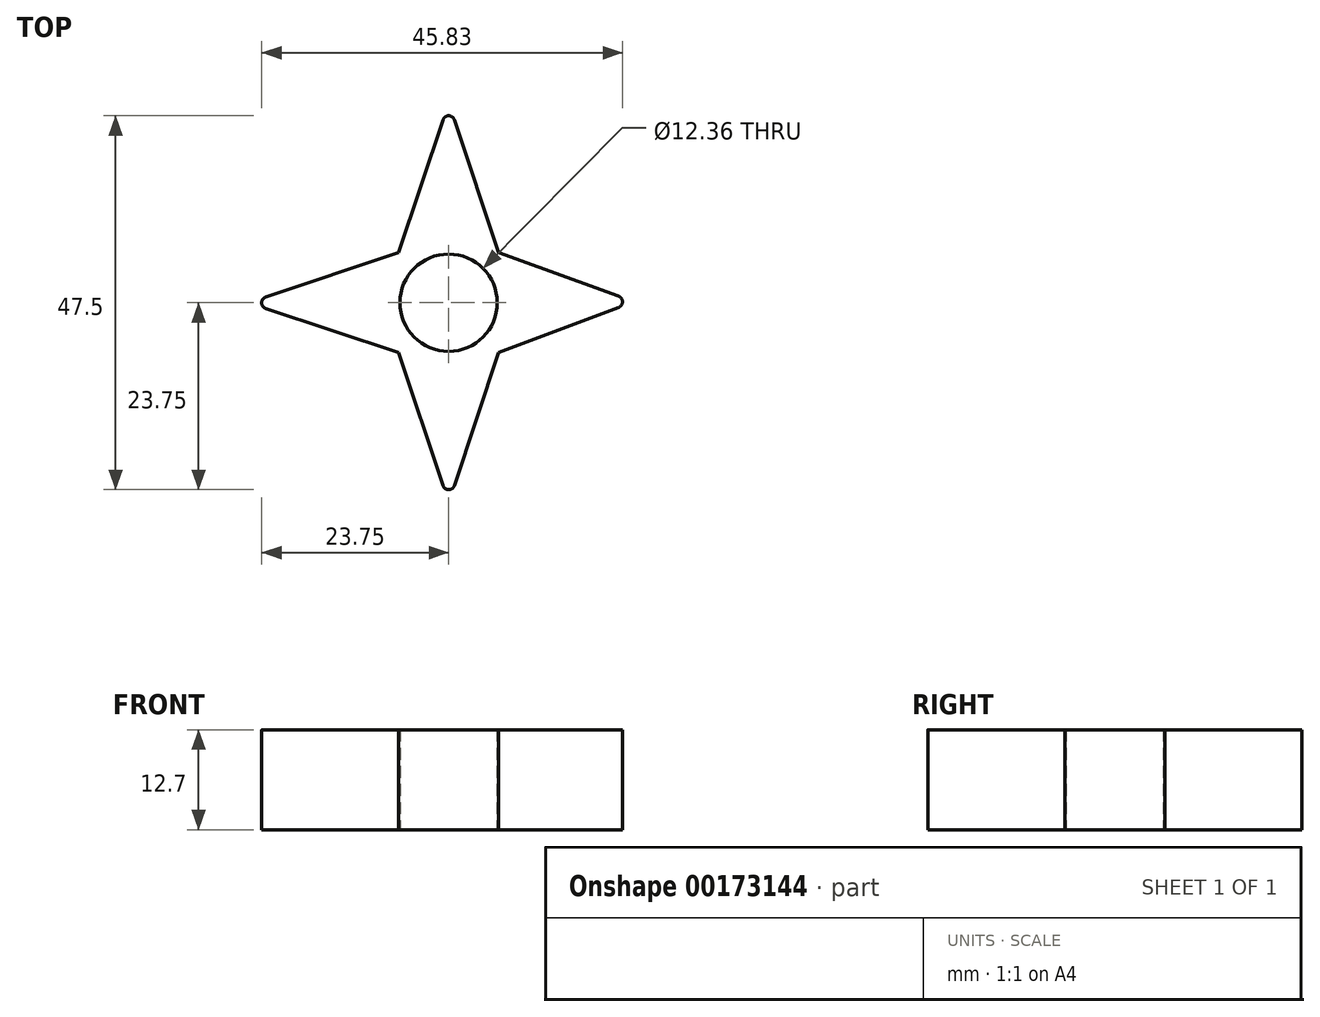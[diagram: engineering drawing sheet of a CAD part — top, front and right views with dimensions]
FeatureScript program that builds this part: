
annotation { "Feature Type Name" : "Feature", "Feature Type Description" : "" }
export const myFeature = defineFeature(function(context is Context, id is Id, definition is map)
    precondition{}
    {
        {
            var Q0;
            Q0=qCreatedBy(makeId("Top.planeOp"),FACE);
            var sketch = newSketch(context, id + "F0", { "sketchPlane" : qUnion([Q0])});
            skLineSegment(sketch, "E0", {"start": v(23.17, 0) * mm, "end": v(23.87, 0) * mm});
            skPoint(sketch, "E1.middle", {"position": v(0, 0) * mm});
            skLineSegment(sketch, "E2", {"start": v(-6.35, 6.35) * mm, "end": v(-25.4, 0) * mm});
            skLineSegment(sketch, "E3", {"start": v(0, 25.4) * mm, "end": v(-6.35, 6.35) * mm});
            skLineSegment(sketch, "E4", {"start": v(0, 25.4) * mm, "end": v(6.35, 6.35) * mm});
            skLineSegment(sketch, "E5", {"start": v(6.35, 6.35) * mm, "end": v(23.87, 0) * mm});
            skLineSegment(sketch, "E6", {"start": v(23.54, 0.14) * mm, "end": v(6.35, -6.35) * mm});
            skLineSegment(sketch, "E7", {"start": v(6.35, -6.35) * mm, "end": v(0, -25.4) * mm});
            skLineSegment(sketch, "E8", {"start": v(0, -25.4) * mm, "end": v(-6.35, -6.35) * mm});
            skLineSegment(sketch, "E9", {"start": v(-6.35, -6.35) * mm, "end": v(-25.4, 0) * mm});
            skCircle(sketch, "E10", {"center": v(0, 0) * mm, "radius": 6.18 * mm});
            skSolve(sketch);
        }
        {
            var Q0;
            Q0=makeQuery(id+"F0.imprint","IMPRINT",FACE,{"disambiguationData":[TD([[makeQuery(id+"F0.imprint","IMPRINT",EDGE,{"derivedFrom":sQuery(id+"F0.wireOp",EDGE,"E2")}),1.0]])]});
            extrude(context, id + "F1", {"entities" : qUnion([Q0]), "depth" : 12.7 * mm});
        }
        {
            var Q0;
            Q0=makeQuery(id+"F1.opExtrude","SWEPT_EDGE",EDGE,{"disambiguationData":[OSD([sQuery(id+"F0.wireOp",EDGE,"E5"),sQuery(id+"F0.wireOp",EDGE,"E6")])]});
            var Q1;
            Q1=makeQuery(id+"F1.opExtrude","SWEPT_EDGE",EDGE,{"disambiguationData":[OSD([sQuery(id+"F0.wireOp",EDGE,"E2"),sQuery(id+"F0.wireOp",EDGE,"E9")])]});
            var Q2;
            Q2=makeQuery(id+"F1.opExtrude","SWEPT_EDGE",EDGE,{"disambiguationData":[OSD([sQuery(id+"F0.wireOp",EDGE,"E3"),sQuery(id+"F0.wireOp",EDGE,"E4")])]});
            var Q3;
            Q3=makeQuery(id+"F1.opExtrude","SWEPT_EDGE",EDGE,{"disambiguationData":[OSD([sQuery(id+"F0.wireOp",EDGE,"E7"),sQuery(id+"F0.wireOp",EDGE,"E8")])]});
            fillet(context, id + "F2", {"entities" : qUnion([Q0, Q1, Q2, Q3]), "radius" : 0.76 * mm, "tangentPropagation" : true, "allowEdgeOverflow" : false});
        }
    });
